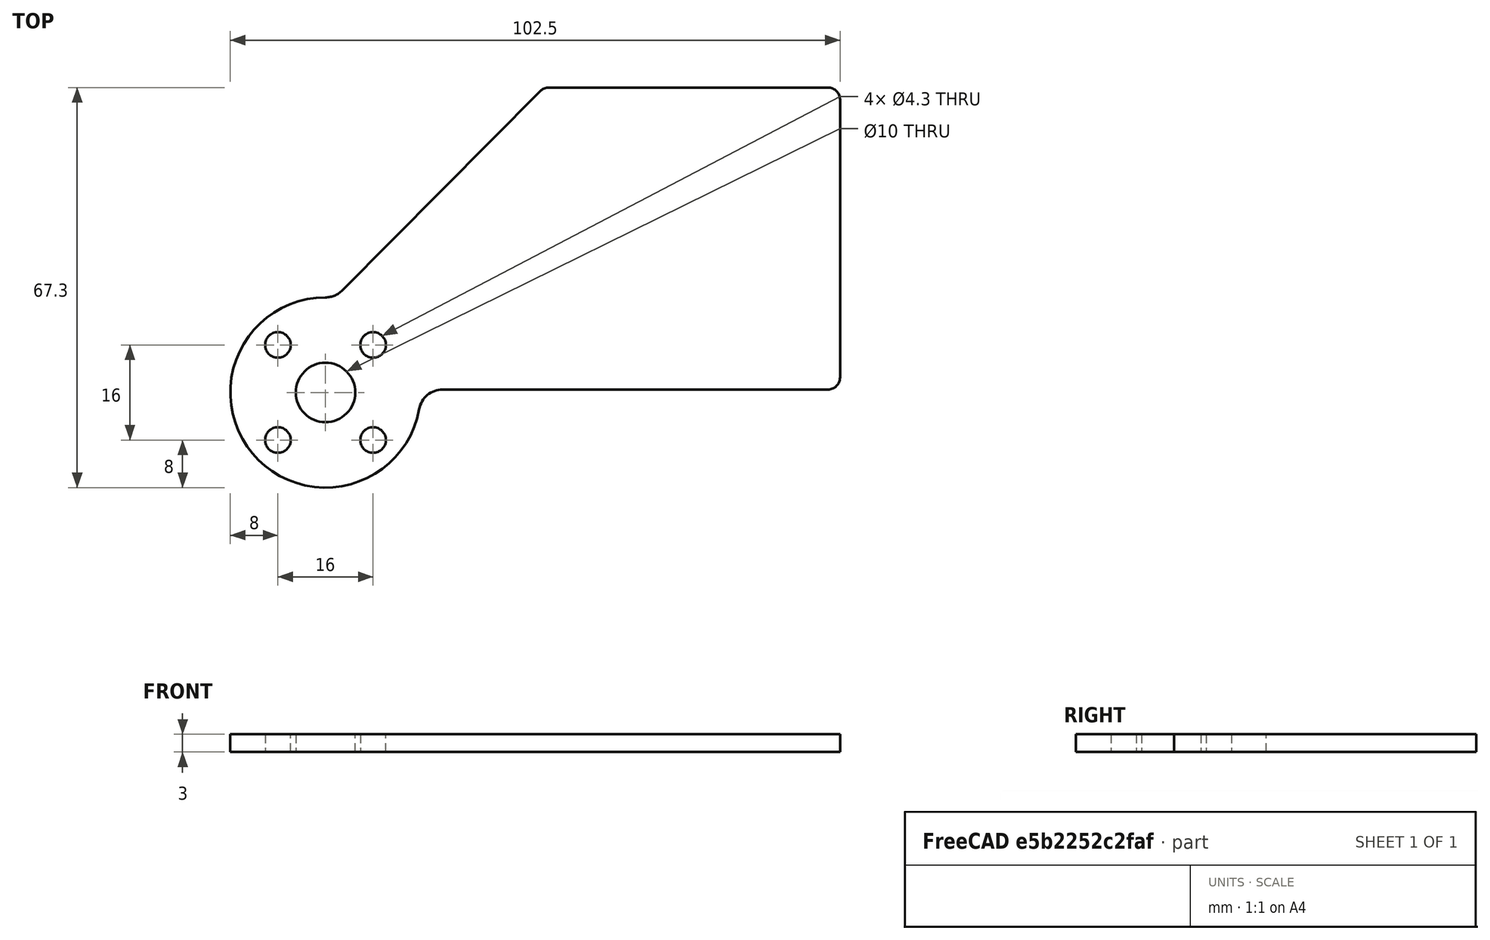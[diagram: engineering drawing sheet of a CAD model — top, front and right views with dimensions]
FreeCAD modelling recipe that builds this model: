
FCSTD DOCUMENT  (FreeCAD 0.21R33675 (Git))
Label: tmaze_door_2in
License: All rights reserved
LicenseURL: http://en.wikipedia.org/wiki/All_rights_reserved
objects: Sketcher::SketchObject×1, Spreadsheet::Sheet×1, PartDesign::Pad×1, PartDesign::Body×1
note: 4 computed .brp shape members not serialized (recipe doc carries the construction recipe); baked Part::Feature solids carry a one-line shape summary decoded from their .brp

FEATURE [Sketcher::SketchObject] Sketch  label="DoorSketch"
  FullyConstrained = true
  MapMode = 5
  Support = -> [XY_Plane]
  expr: Constraints[11] = Spreadsheet.DoorFilletRadius
  expr: Constraints[1] = Spreadsheet.DoorHubDiameter
  expr: Constraints[29] = Spreadsheet.DoorToMazeFloorMargin
  expr: Constraints[34] = Spreadsheet.DoorHubFilletRadius
  expr: Constraints[3] = Spreadsheet.DoorLength
  expr: Constraints[40] = Spreadsheet.ServoSplineToMazeFloorDistance
  expr: Constraints[58] = Spreadsheet.ServoHubMountThruHoleDiameter
  expr: Constraints[59] = Spreadsheet.ServoHubMountHoleSpacing
  expr: Constraints[5] = Spreadsheet.DoorHeight
  expr: Constraints[61] = Spreadsheet.ServoHubCenterHoleDiameter
  sketch-geometry (26):
    g0: Circle CenterX=0 CenterY=0 CenterZ=0 NormalX=0 NormalY=0 NormalZ=1 AngleXU=0 Radius=16
    g1: LineSegment StartX=36.7 StartY=0.5 StartZ=0 EndX=84.5 EndY=0.5 EndZ=0
    g2: LineSegment StartX=86.5 StartY=2.5 StartZ=0 EndX=86.5 EndY=49.3 EndZ=0
    g3: LineSegment StartX=84.5 StartY=51.3 StartZ=0 EndX=37.5329 EndY=51.3 EndZ=0
    g4: LineSegment StartX=2.83909 StartY=17.1823 StartZ=0 EndX=36.1133 EndY=50.7089 EndZ=0
    g5: ArcOfCircle CenterX=84.5 CenterY=2.5 CenterZ=0 NormalX=0 NormalY=0 NormalZ=1 AngleXU=0 Radius=2 StartAngle=4.71239 EndAngle=6.28319
    g6: GeomPoint X=86.5 Y=0.5 Z=0
    g7: ArcOfCircle CenterX=84.5 CenterY=49.3 CenterZ=0 NormalX=0 NormalY=0 NormalZ=1 AngleXU=0 Radius=2 StartAngle=1.1e-15 EndAngle=1.5708
    g8: GeomPoint X=86.5 Y=51.3 Z=0
    g9: LineSegment StartX=36.7 StartY=51.3 StartZ=0 EndX=36.7 EndY=0.5 EndZ=0
    g10: ArcOfCircle CenterX=37.5329 CenterY=49.3 CenterZ=0 NormalX=0 NormalY=0 NormalZ=1 AngleXU=0 Radius=2 StartAngle=1.5708 EndAngle=2.35997
    g11: GeomPoint X=36.7 Y=51.3 Z=0
    g12: ArcOfCircle CenterX=0 CenterY=0 CenterZ=0 NormalX=0 NormalY=0 NormalZ=1 AngleXU=0 Radius=16 StartAngle=1.5708 EndAngle=6.10728
    g13: LineSegment StartX=36.7 StartY=0 StartZ=0 EndX=36.7 EndY=0.5 EndZ=0
    g14: LineSegment StartX=36.7 StartY=0.5 StartZ=0 EndX=19.6914 EndY=0.5 EndZ=0
    g15: ArcOfCircle CenterX=19.6914 CenterY=-3.5 CenterZ=0 NormalX=0 NormalY=0 NormalZ=1 AngleXU=0 Radius=4 StartAngle=1.5708 EndAngle=2.96569
    g16: ArcOfCircle CenterX=5e-16 CenterY=20 CenterZ=0 NormalX=0 NormalY=0 NormalZ=1 AngleXU=0 Radius=4 StartAngle=4.71239 EndAngle=5.50156
    g17: LineSegment StartX=-8 StartY=8 StartZ=0 EndX=8 EndY=8 EndZ=0
    g18: LineSegment StartX=8 StartY=8 StartZ=0 EndX=8 EndY=-8 EndZ=0
    g19: LineSegment StartX=8 StartY=-8 StartZ=0 EndX=-8 EndY=-8 EndZ=0
    g20: LineSegment StartX=-8 StartY=-8 StartZ=0 EndX=-8 EndY=8 EndZ=0
    g21: Circle CenterX=-8 CenterY=8 CenterZ=0 NormalX=0 NormalY=0 NormalZ=1 AngleXU=0 Radius=2.15
    g22: Circle CenterX=8 CenterY=8 CenterZ=0 NormalX=0 NormalY=0 NormalZ=1 AngleXU=0 Radius=2.15
    g23: Circle CenterX=-8 CenterY=-8 CenterZ=0 NormalX=0 NormalY=0 NormalZ=1 AngleXU=0 Radius=2.15
    g24: Circle CenterX=8 CenterY=-8 CenterZ=0 NormalX=0 NormalY=0 NormalZ=1 AngleXU=0 Radius=2.15
    g25: Circle CenterX=0 CenterY=0 CenterZ=0 NormalX=0 NormalY=0 NormalZ=1 AngleXU=0 Radius=5
  constraints (62):
    c: Coincident(g0,g-1)
    c: Diameter(g0) = 32
    c: Horizontal(g1)
    c: DistanceX(g1,g6) = 49.8
    c: Vertical(g2)
    c: DistanceY(g6,g8) = 50.8
    c: Horizontal(g3)
    c: PointOnObject(g6,g1)
    c: PointOnObject(g6,g2)
    c: Tangent(g1,g5) = -1.5708
    c: Tangent(g2,g5) = -1.5708
    c: Radius(g5) = 2
    c: PointOnObject(g8,g3)
    c: PointOnObject(g8,g2)
    c: Tangent(g3,g7) = -1.5708
    c: Tangent(g2,g7) = -1.5708
    c: Equal(g5,g7)
    c: Coincident(g9,g11)
    c: Vertical(g9)
    c: PointOnObject(g11,g4)
    c: PointOnObject(g11,g3)
    c: Tangent(g4,g10) = 1.5708
    c: Tangent(g3,g10) = -1.5708
    c: Equal(g7,g10)
    c: Coincident(g12,g0)
    c: PointOnObject(g12,g0)
    c: PointOnObject(g13,g-1)
    c: Vertical(g13)
    c: Coincident(g13,g1)
    c: DistanceY(g13,g13) = 0.5
    c: Coincident(g14,g1)
    c: Horizontal(g14)
    c: Tangent(g15,g14) = -1.5708
    c: Tangent(g15,g12) = 1.5708
    c: Radius(g15) = 4
    c: Tangent(g12,g16) = 1.5708
    c: Tangent(g4,g16) = -1.5708
    c: Equal(g16,g15)
    c: PointOnObject(g12,g-2)
    c: Coincident(g9,g1)
    c: DistanceX(g12,g1) = 36.7
    c: Coincident(g17,g18)
    c: Coincident(g18,g19)
    c: Coincident(g19,g20)
    c: Coincident(g20,g17)
    c: Horizontal(g17)
    c: Horizontal(g19)
    c: Vertical(g18)
    c: Vertical(g20)
    c: Symmetric(g17,g18,g12)
    c: Equal(g20,g17)
    c: Coincident(g21,g17)
    c: Coincident(g22,g17)
    c: Coincident(g23,g19)
    c: Coincident(g24,g18)
    c: Equal(g21,g22)
    c: Equal(g22,g24)
    c: Equal(g24,g23)
    c: Diameter(g21) = 4.3
    c: DistanceX(g17,g17) = 16
    c: Coincident(g25,g12)
    c: Diameter(g25) = 10
FEATURE [Spreadsheet::Sheet] Spreadsheet
  cells = A2='Servo Hub Parameters; A3='ServoHubDiameter; B3(ServoHubDiameter)==32 mm; A4='ServoHubMountHoleSpacing; B4(ServoHubMountHoleSpacing)==16 mm; A5='ServoHubMountThruHoleDiameter; B5(ServoHubMountThruHoleDiameter)==4.3 mm; A6='ServoHubCenterHoleDiameter; B6(ServoHubCenterHoleDiameter)==10 mm; A7='ServoSplineToServoMountHoleDistance; B7(ServoSplineToServoMountHoleDistance)==14.2 mm; A8='ServoMountHoleToBracketBndryDistance; B8(ServoMountHoleToBracketBndryDistance)==3.5 mm; A9='ServoMarginToMountPlate; B9(ServoMarginToMountPlate)==10 mm; A10='MountPlateThickness; B10(MountPlateThickness)==9 mm; A11='MazeWidth; B11(MazeWidth)==2 in; A14='Design Parameters; A15='DoorHubDiameter; B15(DoorHubDiameter)==ServoHubDiameter; A16='DoorToMazeFloorMargin; B16(DoorToMazeFloorMargin)==0.5 mm; A17='DoorToMazeWallMargin; B17(DoorToMazeWallMargin)==1 mm; A18='ServoSplineToMazeFloorDistance; B18(ServoSplineToMazeFloorDistance)==ServoSplineToServoMountHoleDistance + ServoMountHoleToBracketBndryDistance + ServoMarginToMountPlate + MountPlateThickness; A19='DoorLength; B19(DoorLength)==MazeWidth - DoorToMazeWallMargin; A20='DoorHeight; B20(DoorHeight)==2 in; A21='DoorFilletRadius; B21(DoorFilletRadius)==2 mm; A22='DoorHubFilletRadius; B22(DoorHubFilletRadius)==4 mm; A23='DoorThickness; B23(DoorThickness)==3 mm
FEATURE [PartDesign::Pad] Pad
  Direction = (0,0,1)
  Length = 3
  Length2 = 10
  Profile = -> Sketch
  ReferenceAxis = -> Sketch [N_Axis]
  Type = 0
  expr: Length = Spreadsheet.DoorThickness
FEATURE [PartDesign::Body] Body
  Group = -> [Sketch,Pad]
  Origin = -> Origin
  Tip = -> Pad
